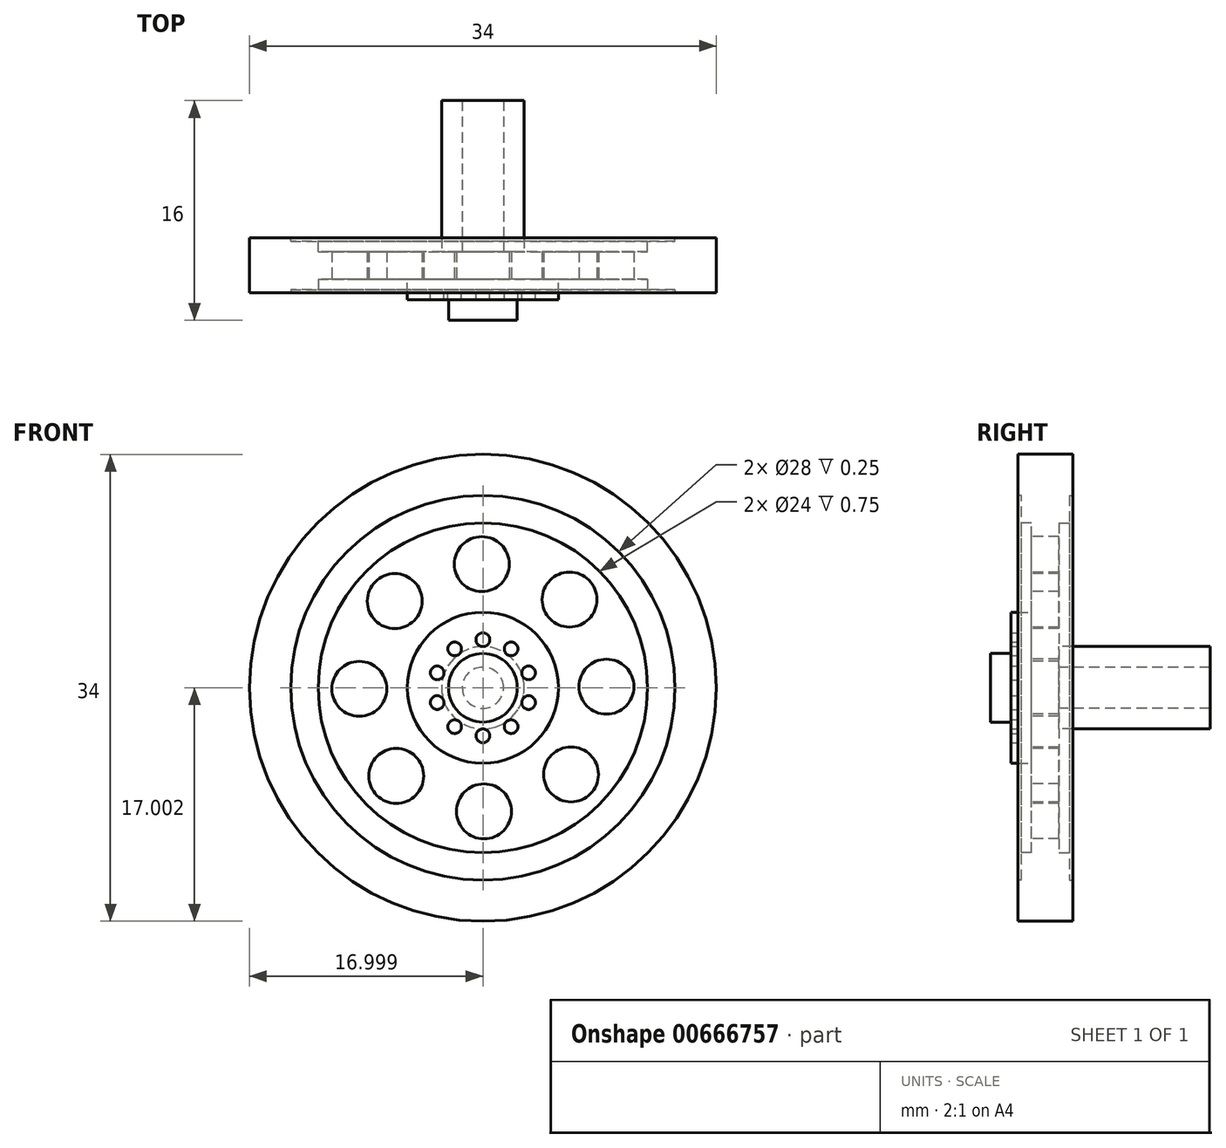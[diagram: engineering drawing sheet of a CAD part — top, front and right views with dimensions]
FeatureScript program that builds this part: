
annotation { "Feature Type Name" : "Feature", "Feature Type Description" : "" }
export const myFeature = defineFeature(function(context is Context, id is Id, definition is map)
    precondition{}
    {
        {
            var Q0;
            Q0=qCreatedBy(makeId("Front.planeOp"),FACE);
            var sketch = newSketch(context, id + "F0", { "sketchPlane" : qUnion([Q0])});
            skCircle(sketch, "E0", {"center": v(-40, 30.11) * mm, "radius": 17 * mm});
            skSolve(sketch);
        }
        {
            var Q0;
            Q0=makeQuery(id+"F0.imprint","IMPRINT",FACE,{"disambiguationData":[TD([[makeQuery(id+"F0.imprint","IMPRINT",EDGE,{"derivedFrom":sQuery(id+"F0.wireOp",EDGE,"E0")}),1.0]])]});
            extrude(context, id + "F1", {"entities" : qUnion([Q0]), "depth" : 4 * mm, "offsetDistance" : 25.4 * mm});
        }
        {
            var Q0;
            Q0=makeQuery(id+"F1.opExtrude","CAP_FACE",FACE,{"disambiguationData":[OSD([sQuery(id+"F0.wireOp",EDGE,"E0")])],"isStart":false});
            var sketch = newSketch(context, id + "F2", { "sketchPlane" : qUnion([Q0])});
            skCircle(sketch, "E1", {"center": v(-40, 30.11) * mm, "radius": 5.5 * mm});
            skCircle(sketch, "E2", {"center": v(-40, 30.11) * mm, "radius": 2.5 * mm});
            skCircle(sketch, "E3", {"center": v(-40, 30.11) * mm, "radius": 12 * mm});
            skCircle(sketch, "E4", {"center": v(-40, 30.11) * mm, "radius": 14 * mm});
            skSolve(sketch);
        }
        {
            var Q0;
            Q0=makeQuery(id+"F2.imprint","IMPRINT",FACE,{"disambiguationData":[TD([[makeQuery(id+"F2.imprint","IMPRINT",EDGE,{"derivedFrom":sQuery(id+"F2.wireOp",EDGE,"E3")}),-1.0]])]});
            extrude(context, id + "F3", {"entities" : qUnion([Q0]), "operationType" : NewBodyOperationType.REMOVE, "oppositeDirection" : true, "depth" : .25 * mm, "offsetDistance" : 25 * mm});
        }
        {
            var Q0;
            Q0=makeQuery(id+"F3.boolean.opBoolean","SPLIT",FACE,{"disambiguationData":[TD([makeQuery(id+"F3.opExtrude","SWEPT_FACE",FACE,{"disambiguationData":[OSD([sQuery(id+"F2.wireOp",EDGE,"E3")])]})])],"derivedFrom":makeQuery(id+"F1.opExtrude","CAP_FACE",FACE,{"disambiguationData":[OSD([sQuery(id+"F0.wireOp",EDGE,"E0")])],"isStart":false})});
            extrude(context, id + "F4", {"entities" : qUnion([Q0]), "operationType" : NewBodyOperationType.REMOVE, "oppositeDirection" : true, "depth" : 1 * mm, "offsetDistance" : 25 * mm});
        }
        {
            var Q0;
            Q0=makeQuery(id+"F4.boolean.opBoolean","COPY",FACE,{"derivedFrom":makeQuery(id+"F4.opExtrude","CAP_FACE",FACE,{"disambiguationData":[OSD([sQuery(id+"F0.wireOp",EDGE,"E0")])],"isStart":false})});
            var sketch = newSketch(context, id + "F5", { "sketchPlane" : qUnion([Q0])});
            skCircle(sketch, "E5", {"center": v(-40, 30.11) * mm, "radius": 5.5 * mm});
            skSolve(sketch);
        }
        {
            var Q0;
            Q0=makeQuery(id+"F5.imprint","IMPRINT",FACE,{"disambiguationData":[TD([[makeQuery(id+"F5.imprint","IMPRINT",EDGE,{"derivedFrom":sQuery(id+"F5.wireOp",EDGE,"E5")}),1.0]])]});
            extrude(context, id + "F6", {"entities" : qUnion([Q0]), "operationType" : NewBodyOperationType.ADD, "depth" : 1 * mm, "offsetDistance" : 25 * mm});
        }
        {
            var Q0;
            Q0=makeQuery(id+"F6.opExtrude","CAP_FACE",FACE,{"disambiguationData":[OSD([sQuery(id+"F5.wireOp",EDGE,"E5")])],"isStart":false});
            var sketch = newSketch(context, id + "F7", { "sketchPlane" : qUnion([Q0])});
            skCircle(sketch, "E6", {"center": v(-40, 30.11) * mm, "radius": 2.5 * mm});
            skSolve(sketch);
        }
        {
            var Q0;
            Q0=makeQuery(id+"F7.imprint","IMPRINT",FACE,{"disambiguationData":[TD([[makeQuery(id+"F7.imprint","IMPRINT",EDGE,{"derivedFrom":sQuery(id+"F7.wireOp",EDGE,"E6")}),1.0]])]});
            extrude(context, id + "F8", {"entities" : qUnion([Q0]), "operationType" : NewBodyOperationType.ADD, "depth" : 2 * mm, "offsetDistance" : 25 * mm});
        }
        {
            var Q0;
            Q0=makeQuery(id+"F6.opExtrude","CAP_FACE",FACE,{"disambiguationData":[OSD([sQuery(id+"F5.wireOp",EDGE,"E5")])],"isStart":false});
            var sketch = newSketch(context, id + "F9", { "sketchPlane" : qUnion([Q0])});
            skCircle(sketch, "E7", {"center": v(-40, 33.61) * mm, "radius": 0.5 * mm});
            skPoint(sketch, "E8.endSnap0", {"position": v(-40, 32.86) * mm});
            skCircle(sketch, "E9.1.0", {"center": v(-42.05, 32.94) * mm, "radius": 0.5 * mm});
            skCircle(sketch, "E9.2.0", {"center": v(-43.32, 31.2) * mm, "radius": 0.5 * mm});
            skCircle(sketch, "E9.3.0", {"center": v(-43.32, 29.03) * mm, "radius": 0.5 * mm});
            skCircle(sketch, "E9.4.0", {"center": v(-42.05, 27.28) * mm, "radius": 0.5 * mm});
            skCircle(sketch, "E9.5.0", {"center": v(-40, 26.61) * mm, "radius": 0.5 * mm});
            skCircle(sketch, "E9.6.0", {"center": v(-37.93, 27.28) * mm, "radius": 0.5 * mm});
            skCircle(sketch, "E9.7.0", {"center": v(-36.66, 29.03) * mm, "radius": 0.5 * mm});
            skCircle(sketch, "E9.8.0", {"center": v(-36.66, 31.2) * mm, "radius": 0.5 * mm});
            skCircle(sketch, "E9.9.0", {"center": v(-37.93, 32.94) * mm, "radius": 0.5 * mm});
            skPoint(sketch, "E9.center", {"position": v(-40, 30.11) * mm});
            skSolve(sketch);
        }
        {
            var Q0;
            Q0=makeQuery(id+"F4.boolean.opBoolean","COPY",FACE,{"derivedFrom":makeQuery(id+"F4.opExtrude","CAP_FACE",FACE,{"disambiguationData":[OSD([sQuery(id+"F0.wireOp",EDGE,"E0")])],"isStart":false})});
            var sketch = newSketch(context, id + "F10", { "sketchPlane" : qUnion([Q0])});
            skCircle(sketch, "E10", {"center": v(-40.07, 39.11) * mm, "radius": 2 * mm});
            skCircle(sketch, "E11.1.0", {"center": v(-46.41, 36.42) * mm, "radius": 2 * mm});
            skCircle(sketch, "E11.2.0", {"center": v(-49, 30.03) * mm, "radius": 2 * mm});
            skCircle(sketch, "E11.3.0", {"center": v(-46.3, 23.7) * mm, "radius": 2 * mm});
            skCircle(sketch, "E11.4.0", {"center": v(-39.91, 21.11) * mm, "radius": 2 * mm});
            skCircle(sketch, "E11.5.0", {"center": v(-33.57, 23.8) * mm, "radius": 2 * mm});
            skCircle(sketch, "E11.6.0", {"center": v(-30.99, 30.2) * mm, "radius": 2 * mm});
            skCircle(sketch, "E11.7.0", {"center": v(-33.68, 36.53) * mm, "radius": 2 * mm});
            skPoint(sketch, "E11.center", {"position": v(-40, 30.11) * mm});
            skSolve(sketch);
        }
        {
            var Q0;
            Q0=makeQuery(id+"F9.imprint","IMPRINT",FACE,{"disambiguationData":[TD([[makeQuery(id+"F9.imprint","IMPRINT",EDGE,{"derivedFrom":sQuery(id+"F9.wireOp",EDGE,"E9.9.0")}),-1.0]])]});
            var Q1;
            Q1=makeQuery(id+"F9.imprint","IMPRINT",FACE,{"disambiguationData":[TD([[makeQuery(id+"F9.imprint","IMPRINT",EDGE,{"derivedFrom":sQuery(id+"F9.wireOp",EDGE,"E7")}),-1.0]])]});
            var Q2;
            Q2=makeQuery(id+"F9.imprint","IMPRINT",FACE,{"disambiguationData":[TD([[makeQuery(id+"F9.imprint","IMPRINT",EDGE,{"derivedFrom":sQuery(id+"F9.wireOp",EDGE,"E9.1.0")}),-1.0]])]});
            var Q3;
            Q3=makeQuery(id+"F9.imprint","IMPRINT",FACE,{"disambiguationData":[TD([[makeQuery(id+"F9.imprint","IMPRINT",EDGE,{"derivedFrom":sQuery(id+"F9.wireOp",EDGE,"E9.2.0")}),-1.0]])]});
            var Q4;
            Q4=makeQuery(id+"F9.imprint","IMPRINT",FACE,{"disambiguationData":[TD([[makeQuery(id+"F9.imprint","IMPRINT",EDGE,{"derivedFrom":sQuery(id+"F9.wireOp",EDGE,"E9.3.0")}),-1.0]])]});
            var Q5;
            Q5=makeQuery(id+"F9.imprint","IMPRINT",FACE,{"disambiguationData":[TD([[makeQuery(id+"F9.imprint","IMPRINT",EDGE,{"derivedFrom":sQuery(id+"F9.wireOp",EDGE,"E9.4.0")}),-1.0]])]});
            var Q6;
            Q6=makeQuery(id+"F9.imprint","IMPRINT",FACE,{"disambiguationData":[TD([[makeQuery(id+"F9.imprint","IMPRINT",EDGE,{"derivedFrom":sQuery(id+"F9.wireOp",EDGE,"E9.5.0")}),-1.0]])]});
            var Q7;
            Q7=makeQuery(id+"F9.imprint","IMPRINT",FACE,{"disambiguationData":[TD([[makeQuery(id+"F9.imprint","IMPRINT",EDGE,{"derivedFrom":sQuery(id+"F9.wireOp",EDGE,"E9.6.0")}),-1.0]])]});
            var Q8;
            Q8=makeQuery(id+"F9.imprint","IMPRINT",FACE,{"disambiguationData":[TD([[makeQuery(id+"F9.imprint","IMPRINT",EDGE,{"derivedFrom":sQuery(id+"F9.wireOp",EDGE,"E9.7.0")}),-1.0]])]});
            var Q9;
            Q9=makeQuery(id+"F9.imprint","IMPRINT",FACE,{"disambiguationData":[TD([[makeQuery(id+"F9.imprint","IMPRINT",EDGE,{"derivedFrom":sQuery(id+"F9.wireOp",EDGE,"E9.8.0")}),-1.0]])]});
            extrude(context, id + "F11", {"entities" : qUnion([Q0, Q1, Q2, Q3, Q4, Q5, Q6, Q7, Q8, Q9]), "operationType" : NewBodyOperationType.ADD, "depth" : .5 * mm, "offsetDistance" : 25 * mm});
        }
        {
            var Q0;
            Q0=makeQuery(id+"F10.imprint","IMPRINT",FACE,{"disambiguationData":[TD([[makeQuery(id+"F10.imprint","IMPRINT",EDGE,{"derivedFrom":sQuery(id+"F10.wireOp",EDGE,"E11.5.0")}),1.0]])]});
            var Q1;
            Q1=makeQuery(id+"F10.imprint","IMPRINT",FACE,{"disambiguationData":[TD([[makeQuery(id+"F10.imprint","IMPRINT",EDGE,{"derivedFrom":sQuery(id+"F10.wireOp",EDGE,"E11.4.0")}),1.0]])]});
            var Q2;
            Q2=makeQuery(id+"F10.imprint","IMPRINT",FACE,{"disambiguationData":[TD([[makeQuery(id+"F10.imprint","IMPRINT",EDGE,{"derivedFrom":sQuery(id+"F10.wireOp",EDGE,"E11.3.0")}),1.0]])]});
            var Q3;
            Q3=makeQuery(id+"F10.imprint","IMPRINT",FACE,{"disambiguationData":[TD([[makeQuery(id+"F10.imprint","IMPRINT",EDGE,{"derivedFrom":sQuery(id+"F10.wireOp",EDGE,"E11.2.0")}),1.0]])]});
            var Q4;
            Q4=makeQuery(id+"F10.imprint","IMPRINT",FACE,{"disambiguationData":[TD([[makeQuery(id+"F10.imprint","IMPRINT",EDGE,{"derivedFrom":sQuery(id+"F10.wireOp",EDGE,"E11.1.0")}),1.0]])]});
            var Q5;
            Q5=makeQuery(id+"F10.imprint","IMPRINT",FACE,{"disambiguationData":[TD([[makeQuery(id+"F10.imprint","IMPRINT",EDGE,{"derivedFrom":sQuery(id+"F10.wireOp",EDGE,"E10")}),1.0]])]});
            var Q6;
            Q6=makeQuery(id+"F10.imprint","IMPRINT",FACE,{"disambiguationData":[TD([[makeQuery(id+"F10.imprint","IMPRINT",EDGE,{"derivedFrom":sQuery(id+"F10.wireOp",EDGE,"E11.7.0")}),1.0]])]});
            var Q7;
            Q7=makeQuery(id+"F10.imprint","IMPRINT",FACE,{"disambiguationData":[TD([[makeQuery(id+"F10.imprint","IMPRINT",EDGE,{"derivedFrom":sQuery(id+"F10.wireOp",EDGE,"E11.6.0")}),1.0]])]});
            extrude(context, id + "F12", {"entities" : qUnion([Q0, Q1, Q2, Q3, Q4, Q5, Q6, Q7]), "operationType" : NewBodyOperationType.REMOVE, "oppositeDirection" : true, "depth" : 25 * mm, "offsetDistance" : 25 * mm});
        }
        {
            var Q0;
            Q0=makeQuery(id+"F1.opExtrude","CAP_FACE",FACE,{"disambiguationData":[OSD([sQuery(id+"F0.wireOp",EDGE,"E0")])],"isStart":true});
            var sketch = newSketch(context, id + "F13", { "sketchPlane" : qUnion([Q0])});
            skCircle(sketch, "E12", {"center": v(40, 30.11) * mm, "radius": 14 * mm});
            skCircle(sketch, "E13", {"center": v(40, 30.11) * mm, "radius": 12 * mm});
            skSolve(sketch);
        }
        {
            var Q0;
            Q0=makeQuery(id+"F13.imprint","IMPRINT",FACE,{"disambiguationData":[TD([[makeQuery(id+"F13.imprint","IMPRINT",EDGE,{"derivedFrom":sQuery(id+"F13.wireOp",EDGE,"E12")}),1.0]])]});
            extrude(context, id + "F14", {"entities" : qUnion([Q0]), "operationType" : NewBodyOperationType.REMOVE, "oppositeDirection" : true, "depth" : .25 * mm, "offsetDistance" : 25 * mm});
        }
        {
            var Q0;
            Q0=makeQuery(id+"F14.boolean.opBoolean","SPLIT",FACE,{"disambiguationData":[TD([makeQuery(id+"F12.boolean.opBoolean","COPY",FACE,{"derivedFrom":makeQuery(id+"F12.opExtrude","SWEPT_FACE",FACE,{"disambiguationData":[OSD([sQuery(id+"F10.wireOp",EDGE,"E10")])]})})])],"derivedFrom":makeQuery(id+"F1.opExtrude","CAP_FACE",FACE,{"disambiguationData":[OSD([sQuery(id+"F0.wireOp",EDGE,"E0")])],"isStart":true})});
            extrude(context, id + "F15", {"entities" : qUnion([Q0]), "operationType" : NewBodyOperationType.REMOVE, "oppositeDirection" : true, "depth" : 1 * mm, "offsetDistance" : 25 * mm});
        }
        {
            var Q0;
            Q0=makeQuery(id+"F15.boolean.opBoolean","COPY",FACE,{"derivedFrom":makeQuery(id+"F15.opExtrude","CAP_FACE",FACE,{"disambiguationData":[OSD([sQuery(id+"F0.wireOp",EDGE,"E0")])],"isStart":false})});
            var sketch = newSketch(context, id + "F16", { "sketchPlane" : qUnion([Q0])});
            skCircle(sketch, "E14", {"center": v(40, 30.11) * mm, "radius": 3 * mm});
            skCircle(sketch, "E15", {"center": v(40, 30.11) * mm, "radius": 1.5 * mm});
            skSolve(sketch);
        }
        {
            var Q0;
            Q0=makeQuery(id+"F16.imprint","IMPRINT",FACE,{"disambiguationData":[TD([[makeQuery(id+"F16.imprint","IMPRINT",EDGE,{"derivedFrom":sQuery(id+"F16.wireOp",EDGE,"E14")}),1.0]])]});
            extrude(context, id + "F17", {"entities" : qUnion([Q0]), "operationType" : NewBodyOperationType.ADD, "depth" : 11 * mm, "offsetDistance" : 25 * mm});
        }
    });
